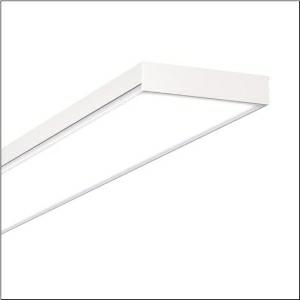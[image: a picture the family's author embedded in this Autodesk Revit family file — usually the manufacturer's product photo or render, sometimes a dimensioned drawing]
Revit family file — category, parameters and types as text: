
# Revit family: apollon_r__31_51mp26wd2341w_af06
name_source: partatom
category: Lighting Fixtures
units: mm (PartAtom-declared; Revit-internal decimal feet)

## family parameters
Cut with Voids When Loaded = No
Host = Face
Light Source = No
Part Type = Normal
Room Calculation Point = No
Round Connector Dimension = Use Diameter
Shared = No

## types (1)
- Apollon® 31 (1 x LED, 4400 lm, 33 W, 3000K)
    Apparent Load = 33 VA
    CIE Flux Codes = 61 87 97 97 100
    Color Rendering = 80
    Color Temperature = 3000K
    Default Elevation = 1800 mm
    Description = Apollon® 31, office luminaire, primary optical cover: micro prismatic cover, of PMMA, light emission: direct distribution, primary light characteristic: symmetric, installation type: surface-mounted, LED, rated luminous flux: 4.400lm, luminous efficacy: 133lm/W, light colour: 830, colour temperature: 3000K, control gear: ECG DALI, with terminal, 5-pole, mains connection: 220..240V, AC, 50/60Hz, rated input power: 33W, housing, of sheet steel, coil coated, traffic white (RAL 9016), length: 1.545mm, width: 200mm, height: 44mm, protection rating (complete): IP20, insulation class (complete): insulation class II (safety insulation), certification: CE, impact resistance: IK02, permissible operating ambient temperature: -20..+40°C, standard: EN 60598-2-22, packaging unit: 1 piece
    Height = 44 mm
    Lamp = 1 x LED
    Lamp Light Flux = 4400 lm
    Lamp Power = 33 W
    Lamp count = 1
    Length = 1545 mm
    Luminous efficacy = 133 lm/W
    Manufacturer = Siteco
    ModVariant = No
    Model = 51MP26WD2341W
    Mounting Place = Ceiling
    Mounting Type = Surface mounted
    Number of Poles = 1
    OnlyDefault = Yes
    Power Factor = 1
    Product Name = Apollon® 31
    Product group = office luminaire | ceiling mounted
    ProductGroupID = 302
    Protection Class = Protection class II
    Protection Degree = IP 20
    RLX_Detail_Level = 1
    RlxData = <blob elided: 20749 chars, md5=c02c0a47>
    Socket = socket
    Standby Power = 0 W
    System Light Flux = 4400 lm
    System Power = 33 W
    Type Comments = Product without accessories
    Type Image = l_1007095.jpg
    URL = http://relux.com
    VarID = ---
    Voltage = 0 V
    Weight = 0.00 kg
    Width = 200 mm  [stored 0.656168 ft]

note: [stored X ft] marks values corroborated as IEEE doubles in the binary element streams (Revit-internal decimal feet)

## geometry (parser evidence)
native form markers: Blend x4, Sweep x9
no freeform markers — native parametric forms only
